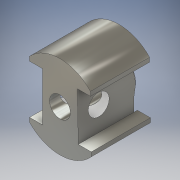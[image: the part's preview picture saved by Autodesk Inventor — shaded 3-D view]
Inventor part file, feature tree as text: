
AUTODESK INVENTOR PART (.ipt)
format: ipt  version: 2017 (Build 210142000, 142)  size: 202,240 bytes
history: native  units: mm
features: extrude x3, sketch x2, projected_geometry x2, fillet x1
ambient origin geometry x8: Origin, YZ Plane, XZ Plane, XY Plane, X Axis, Y Axis, Z Axis, Center Point
bodies: Body1 (feature_tree)
feature tree (8):
  sketch  "Sketch1"  dims[d0=24.0mm d2=3.75mm]
  extrude  "Extrusion3"  Depth=3.75mm
  extrude  "Extrusion5"  Depth=2.0mm
  sketch  "Sketch2"  dims[d3=3.75mm d5=3.75mm d6=3.75mm d28=8.75mm d29=14.0mm d31=1.212034mm d32=1.212034mm d33=6.0mm d34=1.212mm d35=1.212mm d45=16.0mm d46=0.0mm d49=9.5mm d50=6.0mm d51=0.182126mm d52=17.0mm d53=0.0mm d54=6.0mm d55=6.0mm d57=0.0mm d58=0.0mm d67=2.0mm]
  extrude  "Extrusion6"  Depth=2.0mm
  fillet  "Fillet1"  Radius=8.75mm
  projected_geometry  "Projected Loop1"
  projected_geometry  "Projected Loop2"
